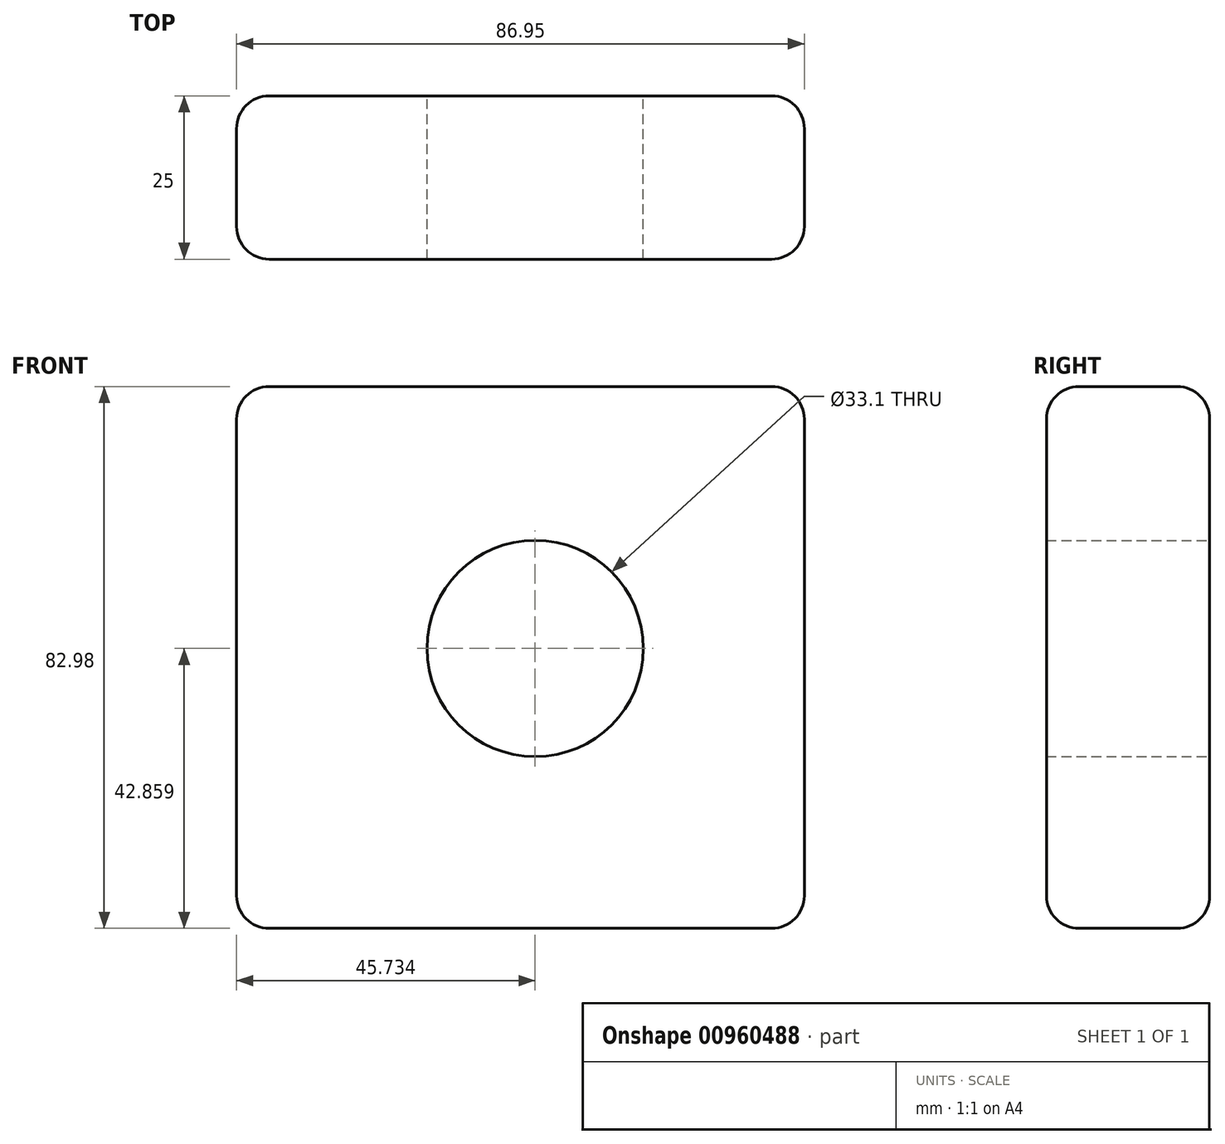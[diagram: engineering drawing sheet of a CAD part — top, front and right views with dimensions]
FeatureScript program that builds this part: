
annotation { "Feature Type Name" : "Feature", "Feature Type Description" : "" }
export const myFeature = defineFeature(function(context is Context, id is Id, definition is map)
    precondition{}
    {
        {
            var Q0;
            Q0=qCreatedBy(makeId("Front.planeOp"),FACE);
            var sketch = newSketch(context, id + "F0", { "sketchPlane" : qUnion([Q0])});
            skLineSegment(sketch, "E0.bottom", {"start": v(-8.4, 48.64) * mm, "end": v(78.54, 48.64) * mm});
            skLineSegment(sketch, "E0.top", {"start": v(-8.4, -34.34) * mm, "end": v(78.54, -34.34) * mm});
            skLineSegment(sketch, "E0.left", {"start": v(-8.4, 48.64) * mm, "end": v(-8.4, -34.34) * mm});
            skLineSegment(sketch, "E0.right", {"start": v(78.54, 48.64) * mm, "end": v(78.54, -34.34) * mm});
            skCircle(sketch, "E1", {"center": v(37.32, 8.52) * mm, "radius": 16.55 * mm});
            skSolve(sketch);
        }
        {
            var Q0;
            Q0=makeQuery(id+"F0.imprint","IMPRINT",FACE,{"disambiguationData":[TD([[makeQuery(id+"F0.imprint","IMPRINT",EDGE,{"derivedFrom":sQuery(id+"F0.wireOp",EDGE,"E0.bottom")}),-1.0]])]});
            extrude(context, id + "F1", {"entities" : qUnion([Q0]), "depth" : 25 * mm, "offsetDistance" : 25 * mm});
        }
        {
            var Q0;
            Q0=makeQuery(id+"F1.opExtrude","SWEPT_FACE",FACE,{"disambiguationData":[OSD([sQuery(id+"F0.wireOp",EDGE,"E0.right")])]});
            var Q1;
            Q1=makeQuery(id+"F1.opExtrude","SWEPT_FACE",FACE,{"disambiguationData":[OSD([sQuery(id+"F0.wireOp",EDGE,"E0.bottom")])]});
            var Q2;
            Q2=makeQuery(id+"F1.opExtrude","SWEPT_FACE",FACE,{"disambiguationData":[OSD([sQuery(id+"F0.wireOp",EDGE,"E0.left")])]});
            var Q3;
            Q3=makeQuery(id+"F1.opExtrude","SWEPT_FACE",FACE,{"disambiguationData":[OSD([sQuery(id+"F0.wireOp",EDGE,"E0.top")])]});
            fillet(context, id + "F2", {"entities" : qUnion([Q0, Q1, Q2, Q3]), "radius" : 5 * mm, "tangentPropagation" : true, "allowEdgeOverflow" : false});
        }
    });
